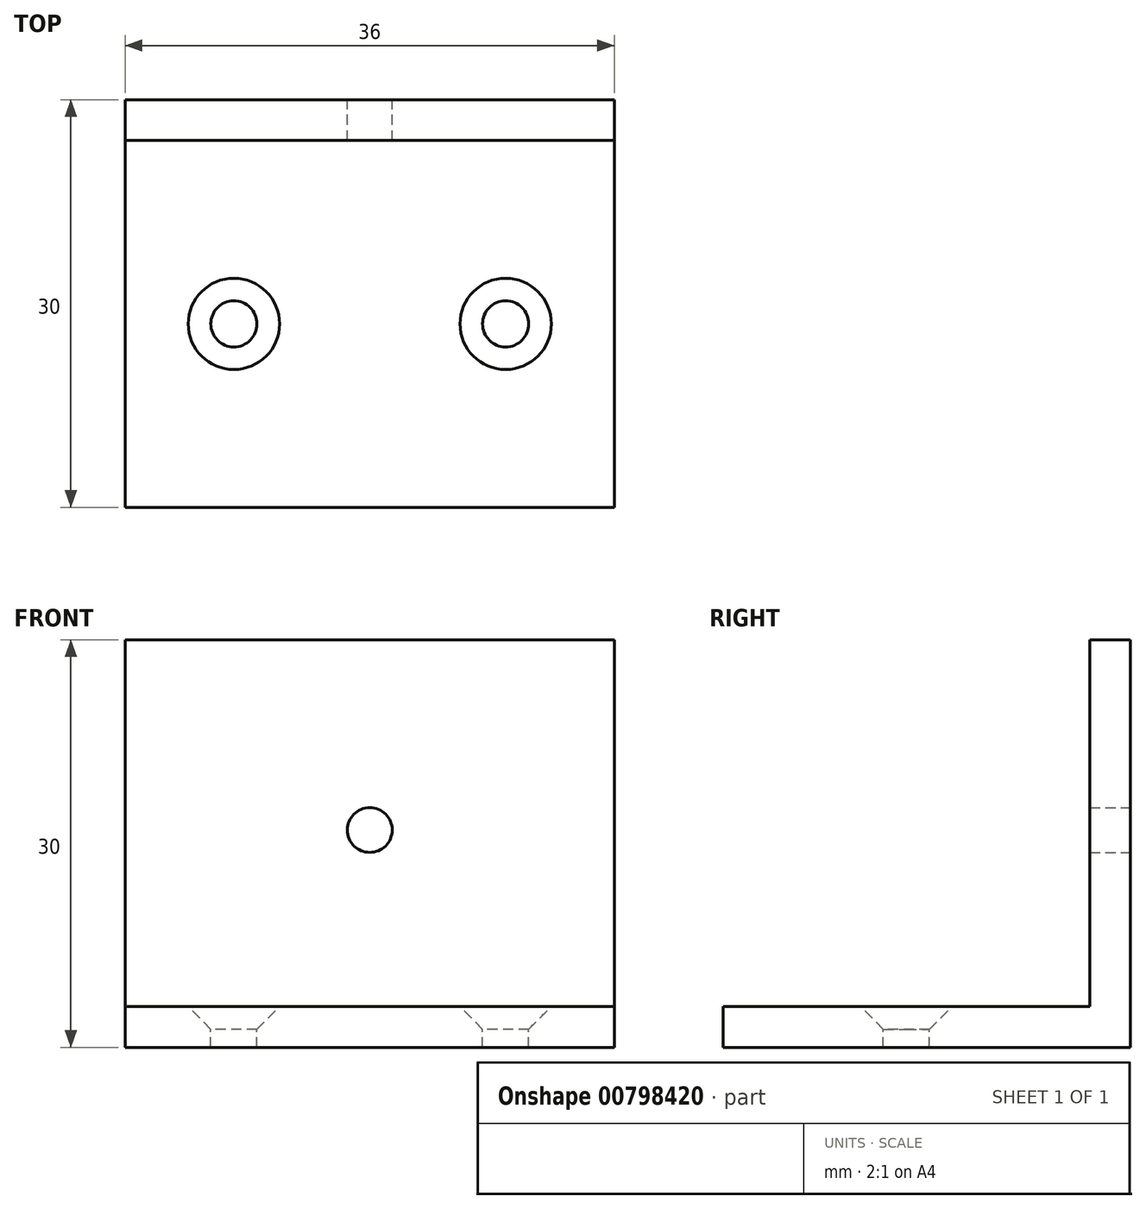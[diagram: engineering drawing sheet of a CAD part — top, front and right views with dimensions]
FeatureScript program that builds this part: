
annotation { "Feature Type Name" : "Feature", "Feature Type Description" : "" }
export const myFeature = defineFeature(function(context is Context, id is Id, definition is map)
    precondition{}
    {
        {
            var Q0;
            Q0=qCreatedBy(makeId("Front.planeOp"),FACE);
            var sketch = newSketch(context, id + "F0", { "sketchPlane" : qUnion([Q0])});
            skLineSegment(sketch, "E0.bottom", {"start": v(-27.7, 29.15) * mm, "end": v(8.3, 29.15) * mm});
            skLineSegment(sketch, "E0.top", {"start": v(-27.7, -0.85) * mm, "end": v(8.3, -0.85) * mm});
            skLineSegment(sketch, "E0.left", {"start": v(-27.7, 29.15) * mm, "end": v(-27.7, -0.85) * mm});
            skLineSegment(sketch, "E0.right", {"start": v(8.3, 29.15) * mm, "end": v(8.3, -0.85) * mm});
            skLineSegment(sketch, "E1", {"start": v(-27.7, 2.15) * mm, "end": v(8.3, 2.15) * mm});
            skLineSegment(sketch, "E2", {"start": v(-9.7, 29.15) * mm, "end": v(-9.7, 2.15) * mm, "construction": true});
            skLineSegment(sketch, "E3", {"start": v(8.3, 15.15) * mm, "end": v(-27.7, 15.15) * mm, "construction": true});
            skPoint(sketch, "E4", {"position": v(-9.7, 15.15) * mm});
            skSolve(sketch);
        }
        {
            var Q0;
            {var subQ0=sQuery(id+"F0.wireOp",EDGE,"E0.top");Q0=makeQuery(id+"F0.imprint","IMPRINT",FACE,{"disambiguationData":[TD([[makeQuery(id+"F0.imprint","IMPRINT",EDGE,{"derivedFrom":subQ0}),1.0]])]});}
            extrude(context, id + "F1", {"entities" : qUnion([Q0]), "depth" : 30 * mm, "offsetDistance" : 25 * mm});
        }
        {
            var Q0;
            Q0 = qSketchRegion(id + "F0", true);
            extrude(context, id + "F2", {"entities" : qUnion([Q0]), "operationType" : NewBodyOperationType.ADD, "depth" : 3 * mm, "offsetDistance" : 25 * mm});
        }
        {
            var Q0;
            Q0=makeQuery(id+"F1.opExtrude","SWEPT_FACE",FACE,{"disambiguationData":[OSD([sQuery(id+"F0.wireOp",EDGE,"E1")])]});
            var sketch = newSketch(context, id + "F3", { "sketchPlane" : qUnion([Q0])});
            skLineSegment(sketch, "E5", {"start": v(-9.7, -30) * mm, "end": v(-9.7, -3) * mm, "construction": true});
            skLineSegment(sketch, "E6", {"start": v(-27.7, -16.5) * mm, "end": v(8.3, -16.5) * mm, "construction": true});
            skLineSegment(sketch, "E7", {"start": v(-19.7, -30) * mm, "end": v(-19.7, -3) * mm, "construction": true});
            skLineSegment(sketch, "E8", {"start": v(0.3, -30) * mm, "end": v(0.3, -3) * mm, "construction": true});
            skPoint(sketch, "E9", {"position": v(-19.7, -16.5) * mm});
            skPoint(sketch, "E10", {"position": v(0.3, -16.5) * mm});
            skSolve(sketch);
        }
        {
            var Q0;
            Q0=sQuery(id+"F3.wireOp",VERTEX,"E9");
            var Q1;
            Q1=sQuery(id+"F3.wireOp",VERTEX,"E10");
            var Q2;
            Q2=makeQuery(id+"F1.opExtrude","SWEPT_BODY",BODY,{"disambiguationData":[OSD([sQuery(id+"F0.wireOp",EDGE,"E0.top"),sQuery(id+"F0.wireOp",EDGE,"E0.left"),sQuery(id+"F0.wireOp",EDGE,"E0.right"),sQuery(id+"F0.wireOp",EDGE,"E1")])]});
            hole(context, id + "F4", {"style" : HoleStyle.C_SINK, "endStyle" : HoleEndStyle.THROUGH, "standardTappedOrClearance" : lookupTablePath({ "fit" : "Normal", "standard" : "ISO", "size" : "M3", "type" : "Clearance" }), "standardBlindInLast" : lookupTablePath({ "fit" : "Normal", "standard" : "ISO", "engagement" : "75%", "pitch" : "0.5 mm", "size" : "M3", "type" : "Clearance & tapped" }), "holeDiameter" : 3.4 * mm, "cSinkDiameter" : 6.72 * mm, "cSinkAngle" : 90 * degree, "majorDiameter" : 5 * mm, "tappedDepth" : 12 * mm, "tapClearance" : 3, "locations" : qUnion([Q0, Q1]), "scope" : qUnion([Q2])});
        }
        {
            var Q0;
            Q0=sQuery(id+"F0.wireOp",VERTEX,"E4");
            var Q1;
            Q1=makeQuery(id+"F1.opExtrude","SWEPT_BODY",BODY,{"disambiguationData":[OSD([sQuery(id+"F0.wireOp",EDGE,"E0.top"),sQuery(id+"F0.wireOp",EDGE,"E0.left"),sQuery(id+"F0.wireOp",EDGE,"E0.right"),sQuery(id+"F0.wireOp",EDGE,"E1")])]});
            hole(context, id + "F5", {"style" : HoleStyle.SIMPLE, "endStyle" : HoleEndStyle.THROUGH, "oppositeDirection" : true, "standardTappedOrClearance" : lookupTablePath({ "standard" : "ISO", "engagement" : "75%", "pitch" : "0.7 mm", "size" : "M4", "type" : "Tapped" }), "standardBlindInLast" : lookupTablePath({ "standard" : "ISO", "fit" : "Normal", "engagement" : "75%", "pitch" : "0.7 mm", "size" : "M4", "type" : "Clearance & tapped" }), "holeDiameter" : 3.3 * mm, "majorDiameter" : 4 * mm, "showTappedDepth" : true, "isTappedThrough" : true, "tappedDepth" : 12 * mm, "tapClearance" : 3, "locations" : qUnion([Q0]), "scope" : qUnion([Q1])});
        }
    });
